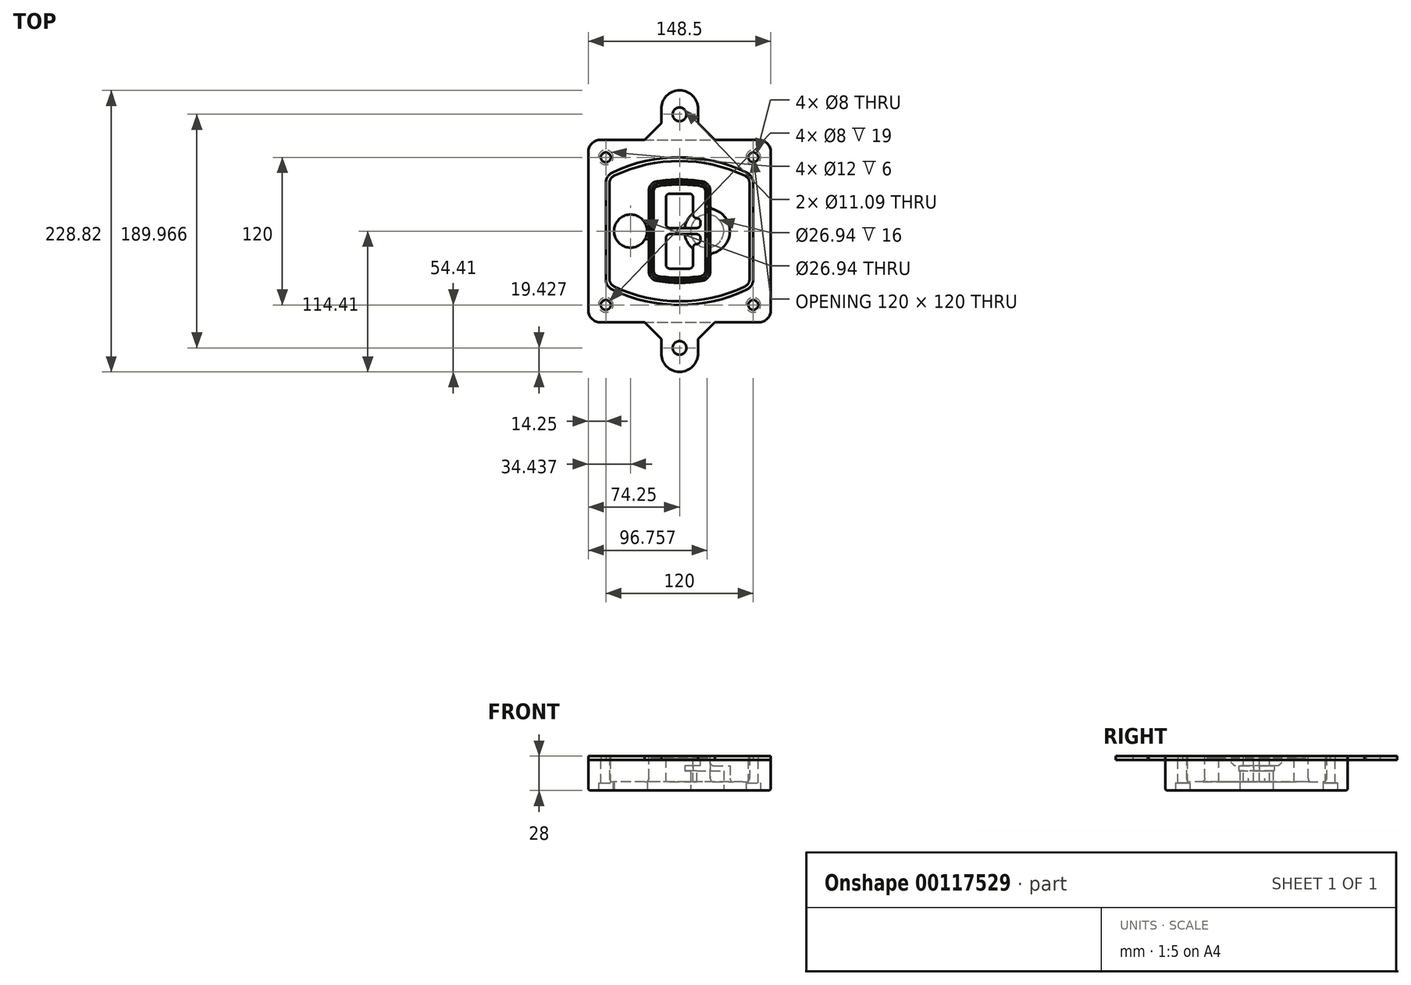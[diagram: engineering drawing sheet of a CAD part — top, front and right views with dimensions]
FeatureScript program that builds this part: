
annotation { "Feature Type Name" : "Feature", "Feature Type Description" : "" }
export const myFeature = defineFeature(function(context is Context, id is Id, definition is map)
    precondition{}
    {
        {
            var Q0;
            Q0=qCreatedBy(makeId("Top.planeOp"),FACE);
            var sketch = newSketch(context, id + "F0", { "sketchPlane" : qUnion([Q0])});
            skPoint(sketch, "E0.rect.middle", {"position": v(0, 0) * mm});
            skLineSegment(sketch, "E1.bottom", {"start": v(-64.25, -74.25) * mm, "end": v(64.25, -74.25) * mm});
            skLineSegment(sketch, "E1.top", {"start": v(-64.25, 74.25) * mm, "end": v(64.25, 74.25) * mm});
            skLineSegment(sketch, "E1.left", {"start": v(-74.25, -64.25) * mm, "end": v(-74.25, 64.25) * mm});
            skLineSegment(sketch, "E1.right", {"start": v(74.25, -64.25) * mm, "end": v(74.25, 64.25) * mm});
            skLineSegment(sketch, "E2", {"start": v(-74.25, 74.25) * mm, "end": v(74.25, -74.25) * mm, "construction": true});
            skLineSegment(sketch, "E3", {"start": v(74.25, 74.25) * mm, "end": v(-74.25, -74.25) * mm, "construction": true});
            skCircle(sketch, "E4", {"center": v(-60, 60) * mm, "radius": 4 * mm});
            skCircle(sketch, "E5", {"center": v(60, 60) * mm, "radius": 4 * mm});
            skCircle(sketch, "E6", {"center": v(60, -60) * mm, "radius": 4 * mm});
            skCircle(sketch, "E7", {"center": v(-60, -60) * mm, "radius": 4 * mm});
            skLineSegment(sketch, "E8", {"start": v(-60, 60) * mm, "end": v(60, 60) * mm, "construction": true});
            skLineSegment(sketch, "E9", {"start": v(60, 60) * mm, "end": v(60, -60) * mm, "construction": true});
            skLineSegment(sketch, "E10", {"start": v(60, -60) * mm, "end": v(-60, -60) * mm, "construction": true});
            skLineSegment(sketch, "E11", {"start": v(-60, -60) * mm, "end": v(-60, 60) * mm, "construction": true});
            skLineSegment(sketch, "E12", {"start": v(-60, 38.83) * mm, "end": v(-60, -38.83) * mm});
            skLineSegment(sketch, "E13", {"start": v(60, 38.83) * mm, "end": v(60, -38.83) * mm});
            skArc(sketch, "E14", {"start": v(54.26, 47.88) * mm, "mid": v(0, 60) * mm, "end": v(-54.26, 47.88) * mm});
            skArc(sketch, "E15", {"start": v(-54.26, -47.88) * mm, "mid": v(0, -60) * mm, "end": v(54.26, -47.88) * mm});
            skLineSegment(sketch, "E16", {"start": v(-60, 0) * mm, "end": v(60, 0) * mm, "construction": true});
            skPoint(sketch, "E17.visualSharp", {"position": v(-60, -45) * mm});
            skArc(sketch, "E17.filletArc", {"start": v(-60, -38.83) * mm, "mid": v(-58.44, -44.2) * mm, "end": v(-54.26, -47.88) * mm});
            skPoint(sketch, "E18.visualSharp", {"position": v(-60, 45) * mm});
            skArc(sketch, "E18.filletArc", {"start": v(-54.26, 47.88) * mm, "mid": v(-58.44, 44.2) * mm, "end": v(-60, 38.83) * mm});
            skPoint(sketch, "E19.visualSharp", {"position": v(60, 45) * mm});
            skArc(sketch, "E19.filletArc", {"start": v(60, 38.83) * mm, "mid": v(58.44, 44.2) * mm, "end": v(54.26, 47.88) * mm});
            skPoint(sketch, "E20.visualSharp", {"position": v(60, -45) * mm});
            skArc(sketch, "E20.filletArc", {"start": v(54.26, -47.88) * mm, "mid": v(58.44, -44.2) * mm, "end": v(60, -38.83) * mm});
            skPoint(sketch, "E21.visualSharp", {"position": v(-74.25, 74.25) * mm});
            skArc(sketch, "E21.filletArc", {"start": v(-64.25, 74.25) * mm, "mid": v(-71.32, 71.32) * mm, "end": v(-74.25, 64.25) * mm});
            skPoint(sketch, "E22.visualSharp", {"position": v(74.25, 74.25) * mm});
            skArc(sketch, "E22.filletArc", {"start": v(74.25, 64.25) * mm, "mid": v(71.32, 71.32) * mm, "end": v(64.25, 74.25) * mm});
            skPoint(sketch, "E23.visualSharp", {"position": v(74.25, -74.25) * mm});
            skArc(sketch, "E23.filletArc", {"start": v(64.25, -74.25) * mm, "mid": v(71.32, -71.32) * mm, "end": v(74.25, -64.25) * mm});
            skPoint(sketch, "E24.visualSharp", {"position": v(-74.25, -74.25) * mm});
            skArc(sketch, "E24.filletArc", {"start": v(-74.25, -64.25) * mm, "mid": v(-71.32, -71.32) * mm, "end": v(-64.25, -74.25) * mm});
            skArc(sketch, "E25.0", {"start": v(57, 38.83) * mm, "mid": v(55.9, 42.58) * mm, "end": v(52.98, 45.17) * mm});
            skLineSegment(sketch, "E25.1", {"start": v(57, 38.83) * mm, "end": v(57, -38.83) * mm});
            skArc(sketch, "E25.2", {"start": v(52.98, -45.17) * mm, "mid": v(55.9, -42.58) * mm, "end": v(57, -38.83) * mm});
            skArc(sketch, "E25.3", {"start": v(-52.98, -45.17) * mm, "mid": v(0, -57) * mm, "end": v(52.98, -45.17) * mm});
            skArc(sketch, "E25.4", {"start": v(-57, -38.83) * mm, "mid": v(-55.9, -42.58) * mm, "end": v(-52.98, -45.17) * mm});
            skArc(sketch, "E25.5", {"start": v(52.98, 45.17) * mm, "mid": v(0, 57) * mm, "end": v(-52.98, 45.17) * mm});
            skLineSegment(sketch, "E25.6", {"start": v(-57, 38.83) * mm, "end": v(-57, -38.83) * mm});
            skArc(sketch, "E25.7", {"start": v(-52.98, 45.17) * mm, "mid": v(-55.9, 42.58) * mm, "end": v(-57, 38.83) * mm});
            skArc(sketch, "E26.0", {"start": v(-55.96, 51.5) * mm, "mid": v(-61.82, 46.33) * mm, "end": v(-64, 38.83) * mm});
            skArc(sketch, "E26.1", {"start": v(55.96, 51.5) * mm, "mid": v(0, 64) * mm, "end": v(-55.96, 51.5) * mm});
            skArc(sketch, "E26.2", {"start": v(64, 38.83) * mm, "mid": v(61.82, 46.33) * mm, "end": v(55.96, 51.5) * mm});
            skLineSegment(sketch, "E26.3", {"start": v(64, 38.83) * mm, "end": v(64, -38.83) * mm});
            skArc(sketch, "E26.4", {"start": v(55.96, -51.5) * mm, "mid": v(61.82, -46.33) * mm, "end": v(64, -38.83) * mm});
            skLineSegment(sketch, "E26.5", {"start": v(-64, 38.83) * mm, "end": v(-64, -38.83) * mm});
            skArc(sketch, "E26.6", {"start": v(-55.96, -51.5) * mm, "mid": v(0, -64) * mm, "end": v(55.96, -51.5) * mm});
            skArc(sketch, "E26.7", {"start": v(-64, -38.83) * mm, "mid": v(-61.82, -46.33) * mm, "end": v(-55.96, -51.5) * mm});
            skSolve(sketch);
        }
        {
            var Q0;
            Q0=makeQuery(id+"F0.imprint","IMPRINT",FACE,{"disambiguationData":[TD([[makeQuery(id+"F0.imprint","IMPRINT",EDGE,{"derivedFrom":sQuery(id+"F0.wireOp",EDGE,"E1.bottom")}),1.0]])]});
            var Q1;
            Q1=makeQuery(id+"F0.imprint","IMPRINT",FACE,{"disambiguationData":[TD([[makeQuery(id+"F0.imprint","IMPRINT",EDGE,{"derivedFrom":sQuery(id+"F0.wireOp",EDGE,"E12")}),1.0]])]});
            var Q2;
            Q2=makeQuery(id+"F0.imprint","IMPRINT",FACE,{"disambiguationData":[TD([[makeQuery(id+"F0.imprint","IMPRINT",EDGE,{"derivedFrom":sQuery(id+"F0.wireOp",EDGE,"E25.0")}),1.0]])]});
            var Q3;
            Q3=makeQuery(id+"F0.imprint","IMPRINT",FACE,{"disambiguationData":[TD([[makeQuery(id+"F0.imprint","IMPRINT",EDGE,{"derivedFrom":sQuery(id+"F0.wireOp",EDGE,"E12")}),-1.0]])]});
            extrude(context, id + "F1", {"entities" : qUnion([Q0, Q1, Q2, Q3]), "oppositeDirection" : true, "depth" : 25 * mm});
        }
        {
            var Q0;
            Q0=makeQuery(id+"F0.imprint","IMPRINT",FACE,{"disambiguationData":[TD([[makeQuery(id+"F0.imprint","IMPRINT",EDGE,{"derivedFrom":sQuery(id+"F0.wireOp",EDGE,"E12")}),1.0]])]});
            extrude(context, id + "F2", {"entities" : qUnion([Q0]), "operationType" : NewBodyOperationType.ADD, "depth" : 3 * mm});
        }
        {
            var Q0;
            Q0=makeQuery(id+"F0.imprint","IMPRINT",FACE,{"disambiguationData":[TD([[makeQuery(id+"F0.imprint","IMPRINT",EDGE,{"derivedFrom":sQuery(id+"F0.wireOp",EDGE,"E25.0")}),1.0]])]});
            extrude(context, id + "F3", {"entities" : qUnion([Q0]), "operationType" : NewBodyOperationType.REMOVE, "oppositeDirection" : true, "depth" : 18 * mm});
        }
        {
            var Q0;
            Q0=makeQuery(id+"F2.opExtrude","CAP_FACE",FACE,{"disambiguationData":[OSD([sQuery(id+"F0.wireOp",EDGE,"E12"),sQuery(id+"F0.wireOp",EDGE,"E13"),sQuery(id+"F0.wireOp",EDGE,"E14"),sQuery(id+"F0.wireOp",EDGE,"E15"),sQuery(id+"F0.wireOp",EDGE,"E17.filletArc"),sQuery(id+"F0.wireOp",EDGE,"E18.filletArc"),sQuery(id+"F0.wireOp",EDGE,"E19.filletArc"),sQuery(id+"F0.wireOp",EDGE,"E20.filletArc"),sQuery(id+"F0.wireOp",EDGE,"E25.0"),sQuery(id+"F0.wireOp",EDGE,"E25.1"),sQuery(id+"F0.wireOp",EDGE,"E25.2"),sQuery(id+"F0.wireOp",EDGE,"E25.3"),sQuery(id+"F0.wireOp",EDGE,"E25.4"),sQuery(id+"F0.wireOp",EDGE,"E25.5"),sQuery(id+"F0.wireOp",EDGE,"E25.6"),sQuery(id+"F0.wireOp",EDGE,"E25.7")])],"isStart":false});
            var sketch = newSketch(context, id + "F4", { "sketchPlane" : qUnion([Q0])});
            skArc(sketch, "E27.0", {"start": v(-18.34, -40.45) * mm, "mid": v(0, -42) * mm, "end": v(18.34, -40.45) * mm});
            skArc(sketch, "E28.0", {"start": v(18.34, 40.45) * mm, "mid": v(0, 42) * mm, "end": v(-18.34, 40.45) * mm});
            skLineSegment(sketch, "E29", {"start": v(-25, 32.57) * mm, "end": v(-25, -32.57) * mm});
            skLineSegment(sketch, "E30", {"start": v(25, 32.57) * mm, "end": v(25, -32.57) * mm});
            skLineSegment(sketch, "E31", {"start": v(-25, 39.1) * mm, "end": v(25, 39.1) * mm, "construction": true});
            skLineSegment(sketch, "E32", {"start": v(-25, -39.1) * mm, "end": v(25, -39.1) * mm, "construction": true});
            skPoint(sketch, "E33.visualSharp", {"position": v(-25, 39.1) * mm});
            skArc(sketch, "E33.filletArc", {"start": v(-18.34, 40.45) * mm, "mid": v(-23.11, 37.73) * mm, "end": v(-25, 32.57) * mm});
            skPoint(sketch, "E34.visualSharp", {"position": v(25, 39.1) * mm});
            skArc(sketch, "E34.filletArc", {"start": v(25, 32.57) * mm, "mid": v(23.11, 37.73) * mm, "end": v(18.34, 40.45) * mm});
            skPoint(sketch, "E35.visualSharp", {"position": v(25, -39.1) * mm});
            skArc(sketch, "E35.filletArc", {"start": v(18.34, -40.45) * mm, "mid": v(23.11, -37.73) * mm, "end": v(25, -32.57) * mm});
            skPoint(sketch, "E36.visualSharp", {"position": v(-25, -39.1) * mm});
            skArc(sketch, "E36.filletArc", {"start": v(-25, -32.57) * mm, "mid": v(-23.11, -37.73) * mm, "end": v(-18.34, -40.45) * mm});
            skArc(sketch, "E37.0", {"start": v(52.98, 45.17) * mm, "mid": v(0, 57) * mm, "end": v(-52.98, 45.17) * mm});
            skArc(sketch, "E37.1", {"start": v(-52.98, 45.17) * mm, "mid": v(-55.9, 42.58) * mm, "end": v(-57, 38.83) * mm});
            skLineSegment(sketch, "E37.2", {"start": v(-57, 38.83) * mm, "end": v(-57, -38.83) * mm});
            skArc(sketch, "E37.3", {"start": v(-57, -38.83) * mm, "mid": v(-55.9, -42.58) * mm, "end": v(-52.98, -45.17) * mm});
            skArc(sketch, "E37.4", {"start": v(-52.98, -45.17) * mm, "mid": v(0, -57) * mm, "end": v(52.98, -45.17) * mm});
            skArc(sketch, "E37.5", {"start": v(52.98, -45.17) * mm, "mid": v(55.9, -42.58) * mm, "end": v(57, -38.83) * mm});
            skLineSegment(sketch, "E37.6", {"start": v(57, 38.83) * mm, "end": v(57, -38.83) * mm});
            skArc(sketch, "E37.7", {"start": v(57, 38.83) * mm, "mid": v(55.9, 42.58) * mm, "end": v(52.98, 45.17) * mm});
            skLineSegment(sketch, "E38.0", {"start": v(23, 32.57) * mm, "end": v(23, -32.57) * mm});
            skArc(sketch, "E38.1", {"start": v(18, -38.48) * mm, "mid": v(21.58, -36.44) * mm, "end": v(23, -32.57) * mm});
            skArc(sketch, "E38.2", {"start": v(-18, -38.48) * mm, "mid": v(0, -40) * mm, "end": v(18, -38.48) * mm});
            skArc(sketch, "E38.3", {"start": v(-23, -32.57) * mm, "mid": v(-21.58, -36.44) * mm, "end": v(-18, -38.48) * mm});
            skLineSegment(sketch, "E38.4", {"start": v(-23, 32.57) * mm, "end": v(-23, -32.57) * mm});
            skArc(sketch, "E38.5", {"start": v(23, 32.57) * mm, "mid": v(21.58, 36.44) * mm, "end": v(18, 38.48) * mm});
            skArc(sketch, "E38.6", {"start": v(-18, 38.48) * mm, "mid": v(-21.58, 36.44) * mm, "end": v(-23, 32.57) * mm});
            skArc(sketch, "E38.7", {"start": v(18, 38.48) * mm, "mid": v(0, 40) * mm, "end": v(-18, 38.48) * mm});
            skArc(sketch, "E39.0", {"start": v(21, 32.57) * mm, "mid": v(20.06, 35.15) * mm, "end": v(17.67, 36.5) * mm});
            skLineSegment(sketch, "E39.1", {"start": v(21, 32.57) * mm, "end": v(21, -32.57) * mm});
            skArc(sketch, "E39.2", {"start": v(17.67, -36.5) * mm, "mid": v(20.06, -35.15) * mm, "end": v(21, -32.57) * mm});
            skArc(sketch, "E39.3", {"start": v(-17.67, -36.5) * mm, "mid": v(0, -38) * mm, "end": v(17.67, -36.5) * mm});
            skArc(sketch, "E39.4", {"start": v(-21, -32.57) * mm, "mid": v(-20.06, -35.15) * mm, "end": v(-17.67, -36.5) * mm});
            skArc(sketch, "E39.5", {"start": v(17.67, 36.5) * mm, "mid": v(0, 38) * mm, "end": v(-17.67, 36.5) * mm});
            skLineSegment(sketch, "E39.6", {"start": v(-21, 32.57) * mm, "end": v(-21, -32.57) * mm});
            skArc(sketch, "E39.7", {"start": v(-17.67, 36.5) * mm, "mid": v(-20.06, 35.15) * mm, "end": v(-21, 32.57) * mm});
            skLineSegment(sketch, "E40", {"start": v(-25, 0) * mm, "end": v(25, 0) * mm, "construction": true});
            skLineSegment(sketch, "E41", {"start": v(-11, 5.5) * mm, "end": v(-11, 27.5) * mm});
            skLineSegment(sketch, "E42", {"start": v(-8, 30.5) * mm, "end": v(8, 30.5) * mm});
            skLineSegment(sketch, "E43", {"start": v(11, 27.5) * mm, "end": v(11, 13.5) * mm});
            skLineSegment(sketch, "E44", {"start": v(14, 10.5) * mm, "end": v(14, 10.5) * mm});
            skLineSegment(sketch, "E45", {"start": v(17, 7.5) * mm, "end": v(17, 5.5) * mm});
            skLineSegment(sketch, "E46", {"start": v(14, 2.5) * mm, "end": v(-8, 2.5) * mm});
            skPoint(sketch, "E47.visualSharp", {"position": v(-11, 30.5) * mm});
            skArc(sketch, "E47.filletArc", {"start": v(-8, 30.5) * mm, "mid": v(-10.12, 29.62) * mm, "end": v(-11, 27.5) * mm});
            skPoint(sketch, "E48.visualSharp", {"position": v(11, 30.5) * mm});
            skArc(sketch, "E48.filletArc", {"start": v(11, 27.5) * mm, "mid": v(10.12, 29.62) * mm, "end": v(8, 30.5) * mm});
            skPoint(sketch, "E49.visualSharp", {"position": v(11, 10.5) * mm});
            skArc(sketch, "E49.filletArc", {"start": v(11, 13.5) * mm, "mid": v(11.88, 11.38) * mm, "end": v(14, 10.5) * mm});
            skPoint(sketch, "E50.visualSharp", {"position": v(17, 10.5) * mm});
            skArc(sketch, "E50.filletArc", {"start": v(17, 7.5) * mm, "mid": v(16.12, 9.62) * mm, "end": v(14, 10.5) * mm});
            skPoint(sketch, "E51.visualSharp", {"position": v(17, 2.5) * mm});
            skArc(sketch, "E51.filletArc", {"start": v(14, 2.5) * mm, "mid": v(16.12, 3.38) * mm, "end": v(17, 5.5) * mm});
            skPoint(sketch, "E52.visualSharp", {"position": v(-11, 2.5) * mm});
            skArc(sketch, "E52.filletArc", {"start": v(-11, 5.5) * mm, "mid": v(-10.12, 3.38) * mm, "end": v(-8, 2.5) * mm});
            skLineSegment(sketch, "E53.0.MirrorCS", {"start": v(14, -2.5) * mm, "end": v(-8, -2.5) * mm});
            skArc(sketch, "E54.0.MirrorCS", {"start": v(-11, -5.5) * mm, "mid": v(-10.12, -3.38) * mm, "end": v(-8, -2.5) * mm});
            skLineSegment(sketch, "E55.0.MirrorCS", {"start": v(-11, -5.5) * mm, "end": v(-11, -27.5) * mm});
            skArc(sketch, "E56.0.MirrorCS", {"start": v(-8, -30.5) * mm, "mid": v(-10.12, -29.62) * mm, "end": v(-11, -27.5) * mm});
            skLineSegment(sketch, "E57.0.MirrorCS", {"start": v(-8, -30.5) * mm, "end": v(8, -30.5) * mm});
            skArc(sketch, "E58.0.MirrorCS", {"start": v(11, -27.5) * mm, "mid": v(10.12, -29.62) * mm, "end": v(8, -30.5) * mm});
            skLineSegment(sketch, "E59.0.MirrorCS", {"start": v(11, -27.5) * mm, "end": v(11, -13.5) * mm});
            skArc(sketch, "E60.0.MirrorCS", {"start": v(11, -13.5) * mm, "mid": v(11.88, -11.38) * mm, "end": v(14, -10.5) * mm});
            skArc(sketch, "E61.0.MirrorCS", {"start": v(17, -7.5) * mm, "mid": v(16.12, -9.62) * mm, "end": v(14, -10.5) * mm});
            skLineSegment(sketch, "E62.0.MirrorCS", {"start": v(17, -7.5) * mm, "end": v(17, -5.5) * mm});
            skArc(sketch, "E63.0.MirrorCS", {"start": v(14, -2.5) * mm, "mid": v(16.12, -3.38) * mm, "end": v(17, -5.5) * mm});
            skSolve(sketch);
        }
        {
            var Q0;
            Q0=makeQuery(id+"F4.imprint","IMPRINT",FACE,{"disambiguationData":[TD([[makeQuery(id+"F4.imprint","IMPRINT",EDGE,{"derivedFrom":sQuery(id+"F4.wireOp",EDGE,"E27.0")}),1.0]])]});
            var Q1;
            Q1=makeQuery(id+"F4.imprint","IMPRINT",FACE,{"disambiguationData":[TD([[makeQuery(id+"F4.imprint","IMPRINT",EDGE,{"derivedFrom":sQuery(id+"F4.wireOp",EDGE,"E38.0")}),-1.0]])]});
            var Q2;
            Q2=makeQuery(id+"F4.imprint","IMPRINT",FACE,{"disambiguationData":[TD([[makeQuery(id+"F4.imprint","IMPRINT",EDGE,{"derivedFrom":sQuery(id+"F4.wireOp",EDGE,"E39.0")}),1.0]])]});
            extrude(context, id + "F5", {"entities" : qUnion([Q0, Q1, Q2]), "operationType" : NewBodyOperationType.ADD, "endBound" : BoundingType.UP_TO_NEXT, "oppositeDirection" : true, "depth" : 25 * mm});
        }
        {
            var Q0;
            Q0=makeQuery(id+"F4.imprint","IMPRINT",FACE,{"disambiguationData":[TD([[makeQuery(id+"F4.imprint","IMPRINT",EDGE,{"derivedFrom":sQuery(id+"F4.wireOp",EDGE,"E38.0")}),-1.0]])]});
            extrude(context, id + "F6", {"entities" : qUnion([Q0]), "operationType" : NewBodyOperationType.REMOVE, "oppositeDirection" : true, "depth" : 2 * mm});
        }
        {
            var Q0;
            Q0=makeQuery(id+"F1.opExtrude","CAP_FACE",FACE,{"disambiguationData":[OSD([sQuery(id+"F0.wireOp",EDGE,"E1.bottom"),sQuery(id+"F0.wireOp",EDGE,"E1.top"),sQuery(id+"F0.wireOp",EDGE,"E1.left"),sQuery(id+"F0.wireOp",EDGE,"E1.right"),sQuery(id+"F0.wireOp",EDGE,"E4"),sQuery(id+"F0.wireOp",EDGE,"E5"),sQuery(id+"F0.wireOp",EDGE,"E6"),sQuery(id+"F0.wireOp",EDGE,"E7"),sQuery(id+"F0.wireOp",EDGE,"E21.filletArc"),sQuery(id+"F0.wireOp",EDGE,"E22.filletArc"),sQuery(id+"F0.wireOp",EDGE,"E23.filletArc"),sQuery(id+"F0.wireOp",EDGE,"E24.filletArc")])],"isStart":false});
            var sketch = newSketch(context, id + "F7", { "sketchPlane" : qUnion([Q0])});
            skCircle(sketch, "E64", {"center": v(22.5, 0) * mm, "radius": 13.47 * mm});
            skCircle(sketch, "E65", {"center": v(-39.81, 0) * mm, "radius": 13.47 * mm});
            skLineSegment(sketch, "E66", {"start": v(74.25, 0) * mm, "end": v(-74.25, 0) * mm});
            skCircle(sketch, "E67", {"center": v(22.5, 0) * mm, "radius": 18.47 * mm});
            skCircle(sketch, "E68", {"center": v(60, -60) * mm, "radius": 6 * mm});
            skCircle(sketch, "E69", {"center": v(-60, -60) * mm, "radius": 6 * mm});
            skCircle(sketch, "E70", {"center": v(-60, 60) * mm, "radius": 6 * mm});
            skCircle(sketch, "E71", {"center": v(60, 60) * mm, "radius": 6 * mm});
            skSolve(sketch);
        }
        {
            var Q0;
            {var subQ1=sQuery(id+"F7.wireOp",EDGE,"E66");var subQ4=sQuery(id+"F7.wireOp",EDGE,"E64");var subQ6=makeQuery(id+"F7.imprint","INTERSECT",VERTEX,{"disambiguationData":[OD(0.0)],"derivedFrom":[subQ4,subQ1]});Q0=makeQuery(id+"F7.imprint","IMPRINT",FACE,{"disambiguationData":[TD([[makeQuery(id+"F7.imprint","IMPRINT",EDGE,{"disambiguationData":[TD([[subQ6,-1.0]])],"derivedFrom":subQ4}),-1.0]])]});}
            var Q1;
            {var subQ0=sQuery(id+"F7.wireOp",EDGE,"E66");var subQ1=sQuery(id+"F7.wireOp",EDGE,"E64");var subQ3=makeQuery(id+"F7.imprint","INTERSECT",VERTEX,{"disambiguationData":[OD(0.0)],"derivedFrom":[subQ1,subQ0]});Q1=makeQuery(id+"F7.imprint","IMPRINT",FACE,{"disambiguationData":[TD([[makeQuery(id+"F7.imprint","IMPRINT",EDGE,{"disambiguationData":[TD([[subQ3,-1.0]])],"derivedFrom":subQ1}),1.0]])]});}
            var Q2;
            {var subQ0=sQuery(id+"F7.wireOp",EDGE,"E66");var subQ1=sQuery(id+"F7.wireOp",EDGE,"E64");var subQ3=makeQuery(id+"F7.imprint","INTERSECT",VERTEX,{"disambiguationData":[OD(0.0)],"derivedFrom":[subQ1,subQ0]});Q2=makeQuery(id+"F7.imprint","IMPRINT",FACE,{"disambiguationData":[TD([[makeQuery(id+"F7.imprint","IMPRINT",EDGE,{"disambiguationData":[TD([[subQ3,1.0]])],"derivedFrom":subQ1}),1.0]])]});}
            var Q3;
            {var subQ1=sQuery(id+"F7.wireOp",EDGE,"E66");var subQ4=sQuery(id+"F7.wireOp",EDGE,"E64");var subQ6=makeQuery(id+"F7.imprint","INTERSECT",VERTEX,{"disambiguationData":[OD(0.0)],"derivedFrom":[subQ4,subQ1]});Q3=makeQuery(id+"F7.imprint","IMPRINT",FACE,{"disambiguationData":[TD([[makeQuery(id+"F7.imprint","IMPRINT",EDGE,{"disambiguationData":[TD([[subQ6,1.0]])],"derivedFrom":subQ4}),-1.0]])]});}
            extrude(context, id + "F8", {"entities" : qUnion([Q0, Q1, Q2, Q3]), "operationType" : NewBodyOperationType.ADD, "oppositeDirection" : true, "depth" : 20 * mm});
        }
        {
            var Q0;
            {var subQ0=sQuery(id+"F7.wireOp",EDGE,"E66");var subQ1=sQuery(id+"F7.wireOp",EDGE,"E64");var subQ3=makeQuery(id+"F7.imprint","INTERSECT",VERTEX,{"disambiguationData":[OD(0.0)],"derivedFrom":[subQ1,subQ0]});Q0=makeQuery(id+"F7.imprint","IMPRINT",FACE,{"disambiguationData":[TD([[makeQuery(id+"F7.imprint","IMPRINT",EDGE,{"disambiguationData":[TD([[subQ3,-1.0]])],"derivedFrom":subQ1}),1.0]])]});}
            var Q1;
            {var subQ0=sQuery(id+"F7.wireOp",EDGE,"E66");var subQ1=sQuery(id+"F7.wireOp",EDGE,"E64");var subQ3=makeQuery(id+"F7.imprint","INTERSECT",VERTEX,{"disambiguationData":[OD(0.0)],"derivedFrom":[subQ1,subQ0]});Q1=makeQuery(id+"F7.imprint","IMPRINT",FACE,{"disambiguationData":[TD([[makeQuery(id+"F7.imprint","IMPRINT",EDGE,{"disambiguationData":[TD([[subQ3,1.0]])],"derivedFrom":subQ1}),1.0]])]});}
            extrude(context, id + "F9", {"entities" : qUnion([Q0, Q1]), "operationType" : NewBodyOperationType.REMOVE, "oppositeDirection" : true, "depth" : 16 * mm});
        }
        {
            var Q0;
            {var subQ0=sQuery(id+"F7.wireOp",EDGE,"E66");var subQ1=sQuery(id+"F7.wireOp",EDGE,"E65");var subQ3=makeQuery(id+"F7.imprint","INTERSECT",VERTEX,{"disambiguationData":[OD(0.0)],"derivedFrom":[subQ1,subQ0]});Q0=makeQuery(id+"F7.imprint","IMPRINT",FACE,{"disambiguationData":[TD([[makeQuery(id+"F7.imprint","IMPRINT",EDGE,{"disambiguationData":[TD([[subQ3,-1.0]])],"derivedFrom":subQ1}),1.0]])]});}
            var Q1;
            {var subQ0=sQuery(id+"F7.wireOp",EDGE,"E66");var subQ1=sQuery(id+"F7.wireOp",EDGE,"E65");var subQ3=makeQuery(id+"F7.imprint","INTERSECT",VERTEX,{"disambiguationData":[OD(0.0)],"derivedFrom":[subQ1,subQ0]});Q1=makeQuery(id+"F7.imprint","IMPRINT",FACE,{"disambiguationData":[TD([[makeQuery(id+"F7.imprint","IMPRINT",EDGE,{"disambiguationData":[TD([[subQ3,1.0]])],"derivedFrom":subQ1}),1.0]])]});}
            extrude(context, id + "F10", {"entities" : qUnion([Q0, Q1]), "operationType" : NewBodyOperationType.REMOVE, "oppositeDirection" : true, "depth" : 25 * mm});
        }
        {
            var Q0;
            Q0=makeQuery(id+"F7.imprint","IMPRINT",FACE,{"disambiguationData":[TD([[makeQuery(id+"F7.imprint","IMPRINT",EDGE,{"derivedFrom":sQuery(id+"F7.wireOp",EDGE,"E68")}),1.0]])]});
            var Q1;
            Q1=makeQuery(id+"F7.imprint","IMPRINT",FACE,{"disambiguationData":[TD([[makeQuery(id+"F7.imprint","IMPRINT",EDGE,{"derivedFrom":makeQuery(id+"F1.opExtrude","CAP_EDGE",EDGE,{"disambiguationData":[OSD([sQuery(id+"F0.wireOp",EDGE,"E5")])],"isStart":false})}),-1.0]])]});
            var Q2;
            Q2=makeQuery(id+"F7.imprint","IMPRINT",FACE,{"disambiguationData":[TD([[makeQuery(id+"F7.imprint","IMPRINT",EDGE,{"derivedFrom":sQuery(id+"F7.wireOp",EDGE,"E69")}),1.0]])]});
            var Q3;
            Q3=makeQuery(id+"F7.imprint","IMPRINT",FACE,{"disambiguationData":[TD([[makeQuery(id+"F7.imprint","IMPRINT",EDGE,{"derivedFrom":makeQuery(id+"F1.opExtrude","CAP_EDGE",EDGE,{"disambiguationData":[OSD([sQuery(id+"F0.wireOp",EDGE,"E4")])],"isStart":false})}),-1.0]])]});
            var Q4;
            Q4=makeQuery(id+"F7.imprint","IMPRINT",FACE,{"disambiguationData":[TD([[makeQuery(id+"F7.imprint","IMPRINT",EDGE,{"derivedFrom":sQuery(id+"F7.wireOp",EDGE,"E70")}),1.0]])]});
            var Q5;
            Q5=makeQuery(id+"F7.imprint","IMPRINT",FACE,{"disambiguationData":[TD([[makeQuery(id+"F7.imprint","IMPRINT",EDGE,{"derivedFrom":makeQuery(id+"F1.opExtrude","CAP_EDGE",EDGE,{"disambiguationData":[OSD([sQuery(id+"F0.wireOp",EDGE,"E7")])],"isStart":false})}),-1.0]])]});
            var Q6;
            Q6=makeQuery(id+"F7.imprint","IMPRINT",FACE,{"disambiguationData":[TD([[makeQuery(id+"F7.imprint","IMPRINT",EDGE,{"derivedFrom":sQuery(id+"F7.wireOp",EDGE,"E71")}),1.0]])]});
            var Q7;
            Q7=makeQuery(id+"F7.imprint","IMPRINT",FACE,{"disambiguationData":[TD([[makeQuery(id+"F7.imprint","IMPRINT",EDGE,{"derivedFrom":makeQuery(id+"F1.opExtrude","CAP_EDGE",EDGE,{"disambiguationData":[OSD([sQuery(id+"F0.wireOp",EDGE,"E6")])],"isStart":false})}),-1.0]])]});
            extrude(context, id + "F11", {"entities" : qUnion([Q0, Q1, Q2, Q3, Q4, Q5, Q6, Q7]), "operationType" : NewBodyOperationType.REMOVE, "oppositeDirection" : true, "depth" : 6 * mm});
        }
        {
            var Q0;
            Q0=makeQuery(id+"F9.boolean.opBoolean","COPY",FACE,{"derivedFrom":makeQuery(id+"F9.opExtrude","CAP_FACE",FACE,{"disambiguationData":[OSD([sQuery(id+"F7.wireOp",EDGE,"E64")])],"isStart":false})});
            var sketch = newSketch(context, id + "F12", { "sketchPlane" : qUnion([Q0])});
            skArc(sketch, "E72.0", {"start": v(11, 14.45) * mm, "mid": v(6.45, 9.13) * mm, "end": v(4.2, 2.5) * mm});
            skArc(sketch, "E72.1", {"start": v(4.2, -2.5) * mm, "mid": v(6.45, -9.13) * mm, "end": v(11, -14.45) * mm});
            skLineSegment(sketch, "E73", {"start": v(4.2, -2.5) * mm, "end": v(14, -2.5) * mm});
            skLineSegment(sketch, "E74.0", {"start": v(14, 2.5) * mm, "end": v(4.2, 2.5) * mm});
            skArc(sketch, "E74.1", {"start": v(14, 2.5) * mm, "mid": v(16.12, 3.38) * mm, "end": v(17, 5.5) * mm});
            skLineSegment(sketch, "E74.2", {"start": v(17, 7.5) * mm, "end": v(17, 5.5) * mm});
            skArc(sketch, "E74.3", {"start": v(17, 7.5) * mm, "mid": v(16.12, 9.62) * mm, "end": v(14, 10.5) * mm});
            skArc(sketch, "E74.4", {"start": v(11, 13.5) * mm, "mid": v(11.88, 11.38) * mm, "end": v(14, 10.5) * mm});
            skLineSegment(sketch, "E74.5", {"start": v(11, 14.45) * mm, "end": v(11, 13.5) * mm});
            skLineSegment(sketch, "E74.7", {"start": v(14, -2.5) * mm, "end": v(4.2, -2.5) * mm});
            skArc(sketch, "E74.8", {"start": v(14, -2.5) * mm, "mid": v(16.12, -3.38) * mm, "end": v(17, -5.5) * mm});
            skLineSegment(sketch, "E74.9", {"start": v(17, -7.5) * mm, "end": v(17, -5.5) * mm});
            skArc(sketch, "E74.10", {"start": v(17, -7.5) * mm, "mid": v(16.12, -9.62) * mm, "end": v(14, -10.5) * mm});
            skArc(sketch, "E74.11", {"start": v(11, -13.5) * mm, "mid": v(11.88, -11.38) * mm, "end": v(14, -10.5) * mm});
            skLineSegment(sketch, "E74.12", {"start": v(11, -14.45) * mm, "end": v(11, -13.5) * mm});
            skPoint(sketch, "E75.orphan", {"position": v(11, -27.5) * mm});
            skPoint(sketch, "E76.orphan", {"position": v(-8, -2.5) * mm});
            skPoint(sketch, "E77.orphan", {"position": v(-8, 2.5) * mm});
            skPoint(sketch, "E78.orphan", {"position": v(11, 27.5) * mm});
            skSolve(sketch);
        }
        {
            var Q0;
            {var subQ7=sQuery(id+"F12.wireOp",EDGE,"E72.0");var subQ14=sQuery(id+"F12.wireOp",EDGE,"E72.1");var subQ16=sQuery(id+"F12.wireOp",EDGE,"E74.1");var subQ18=sQuery(id+"F12.wireOp",EDGE,"E74.8");Q0=qUnion([makeQuery(id+"F12.imprint","IMPRINT",FACE,{"disambiguationData":[TD([[makeQuery(id+"F12.imprint","IMPRINT",EDGE,{"derivedFrom":subQ7}),1.0]])]}),makeQuery(id+"F12.imprint","IMPRINT",FACE,{"disambiguationData":[TD([[makeQuery(id+"F12.imprint","IMPRINT",EDGE,{"derivedFrom":subQ14}),1.0]])]}),makeQuery(id+"F12.imprint","IMPRINT",FACE,{"disambiguationData":[TD([[makeQuery(id+"F12.imprint","IMPRINT",EDGE,{"derivedFrom":subQ16}),1.0]])]}),makeQuery(id+"F12.imprint","IMPRINT",FACE,{"disambiguationData":[TD([[makeQuery(id+"F12.imprint","IMPRINT",EDGE,{"derivedFrom":subQ18}),-1.0]])]})]);}
            var Q1;
            Q1=makeQuery(id+"F5.boolean.opBoolean","SPLIT",FACE,{"disambiguationData":[TD([makeQuery(id+"F5.opExtrude","SWEPT_FACE",FACE,{"disambiguationData":[OSD([sQuery(id+"F4.wireOp",EDGE,"E41")])]})])],"derivedFrom":makeQuery(id+"F3.boolean.opBoolean","COPY",FACE,{"derivedFrom":makeQuery(id+"F3.opExtrude","CAP_FACE",FACE,{"disambiguationData":[OSD([sQuery(id+"F0.wireOp",EDGE,"E25.0"),sQuery(id+"F0.wireOp",EDGE,"E25.1"),sQuery(id+"F0.wireOp",EDGE,"E25.2"),sQuery(id+"F0.wireOp",EDGE,"E25.3"),sQuery(id+"F0.wireOp",EDGE,"E25.4"),sQuery(id+"F0.wireOp",EDGE,"E25.5"),sQuery(id+"F0.wireOp",EDGE,"E25.6"),sQuery(id+"F0.wireOp",EDGE,"E25.7")])],"isStart":false})})});
            extrude(context, id + "F13", {"entities" : qUnion([Q0]), "operationType" : NewBodyOperationType.REMOVE, "endBound" : BoundingType.UP_TO_SURFACE, "endBoundEntityFace" : qUnion([Q1]), "depth" : 25 * mm});
        }
        {
            var Q0;
            Q0=makeQuery(id+"F3.boolean.opBoolean","COPY",EDGE,{"derivedFrom":makeQuery(id+"F3.opExtrude","CAP_EDGE",EDGE,{"disambiguationData":[OSD([sQuery(id+"F0.wireOp",EDGE,"E25.6")])],"isStart":false})});
            var Q1;
            Q1=makeQuery(id+"F8.boolean.opBoolean","INTERSECT",EDGE,{"derivedFrom":[makeQuery(id+"F5.opExtrude","SWEPT_FACE",FACE,{"disambiguationData":[OSD([sQuery(id+"F4.wireOp",EDGE,"E30")])]}),makeQuery(id+"F8.opExtrude","CAP_FACE",FACE,{"disambiguationData":[OSD([sQuery(id+"F7.wireOp",EDGE,"E67")])],"isStart":false})]});
            var Q2;
            Q2=makeQuery(id+"F8.boolean.opBoolean","INTERSECT",EDGE,{"disambiguationData":[OD(1.0)],"derivedFrom":[makeQuery(id+"F5.opExtrude","SWEPT_FACE",FACE,{"disambiguationData":[OSD([sQuery(id+"F4.wireOp",EDGE,"E30")])]}),makeQuery(id+"F8.opExtrude","SWEPT_FACE",FACE,{"disambiguationData":[OSD([sQuery(id+"F7.wireOp",EDGE,"E67")])]})]});
            var Q3;
            {var subQ0=sQuery(id+"F4.wireOp",EDGE,"E30");Q3=makeQuery(id+"F8.boolean.opBoolean","SPLIT",EDGE,{"disambiguationData":[TD([makeQuery(id+"F5.opExtrude","SWEPT_FACE",FACE,{"disambiguationData":[OSD([sQuery(id+"F4.wireOp",EDGE,"E35.filletArc")])]})])],"derivedFrom":makeQuery(id+"F5.opExtrude","CAP_EDGE",EDGE,{"disambiguationData":[OSD([subQ0])],"isStart":false})});}
            var Q4;
            {var subQ0=sQuery(id+"F0.wireOp",EDGE,"E25.7");var subQ1=sQuery(id+"F0.wireOp",EDGE,"E25.1");var subQ2=sQuery(id+"F0.wireOp",EDGE,"E25.6");var subQ3=sQuery(id+"F0.wireOp",EDGE,"E25.5");var subQ4=sQuery(id+"F0.wireOp",EDGE,"E25.4");var subQ5=sQuery(id+"F0.wireOp",EDGE,"E25.0");var subQ6=sQuery(id+"F0.wireOp",EDGE,"E25.2");var subQ7=sQuery(id+"F0.wireOp",EDGE,"E25.3");Q4=makeQuery(id+"F8.boolean.opBoolean","INTERSECT",EDGE,{"derivedFrom":[makeQuery(id+"F5.boolean.opBoolean","SPLIT",FACE,{"disambiguationData":[TD([makeQuery(id+"F2.opExtrude","SWEPT_FACE",FACE,{"disambiguationData":[OSD([subQ5])]})])],"derivedFrom":makeQuery(id+"F3.boolean.opBoolean","COPY",FACE,{"derivedFrom":makeQuery(id+"F3.opExtrude","CAP_FACE",FACE,{"disambiguationData":[OSD([subQ5,subQ1,subQ6,subQ7,subQ4,subQ3,subQ2,subQ0])],"isStart":false})})}),makeQuery(id+"F8.opExtrude","SWEPT_FACE",FACE,{"disambiguationData":[OSD([sQuery(id+"F7.wireOp",EDGE,"E67")])]})]});}
            var Q5;
            Q5=makeQuery(id+"F8.boolean.opBoolean","INTERSECT",EDGE,{"disambiguationData":[OD(0.0)],"derivedFrom":[makeQuery(id+"F5.opExtrude","SWEPT_FACE",FACE,{"disambiguationData":[OSD([sQuery(id+"F4.wireOp",EDGE,"E30")])]}),makeQuery(id+"F8.opExtrude","SWEPT_FACE",FACE,{"disambiguationData":[OSD([sQuery(id+"F7.wireOp",EDGE,"E67")])]})]});
            fillet(context, id + "F14", {"entities" : qUnion([Q0, Q1, Q2, Q3, Q4, Q5]), "radius" : 3 * mm, "tangentPropagation" : true, "allowEdgeOverflow" : false});
        }
        {
            var Q0;
            Q0=makeQuery(id+"F1.opExtrude","CAP_EDGE",EDGE,{"disambiguationData":[OSD([sQuery(id+"F0.wireOp",EDGE,"E1.bottom")])],"isStart":false});
            fillet(context, id + "F15", {"entities" : qUnion([Q0]), "radius" : 2 * mm, "tangentPropagation" : true, "allowEdgeOverflow" : false});
        }
        {
            var Q0;
            {var subQ0=sQuery(id+"F0.wireOp",EDGE,"E22.filletArc");var subQ1=sQuery(id+"F0.wireOp",EDGE,"E7");var subQ2=sQuery(id+"F0.wireOp",EDGE,"E6");var subQ3=sQuery(id+"F0.wireOp",EDGE,"E5");var subQ4=sQuery(id+"F0.wireOp",EDGE,"E4");var subQ5=sQuery(id+"F0.wireOp",EDGE,"E1.bottom");var subQ6=sQuery(id+"F0.wireOp",EDGE,"E21.filletArc");var subQ7=sQuery(id+"F0.wireOp",EDGE,"E1.top");var subQ8=sQuery(id+"F0.wireOp",EDGE,"E1.left");var subQ9=sQuery(id+"F0.wireOp",EDGE,"E1.right");var subQ10=sQuery(id+"F0.wireOp",EDGE,"E23.filletArc");var subQ11=sQuery(id+"F0.wireOp",EDGE,"E24.filletArc");Q0=makeQuery(id+"F2.boolean.opBoolean","SPLIT",FACE,{"disambiguationData":[TD([makeQuery(id+"F1.opExtrude","SWEPT_FACE",FACE,{"disambiguationData":[OSD([subQ5])]})])],"derivedFrom":makeQuery(id+"F1.opExtrude","CAP_FACE",FACE,{"disambiguationData":[OSD([subQ5,subQ7,subQ8,subQ9,subQ4,subQ3,subQ2,subQ1,subQ6,subQ0,subQ10,subQ11])],"isStart":true})});}
            var sketch = newSketch(context, id + "F16", { "sketchPlane" : qUnion([Q0])});
            skLineSegment(sketch, "E79", {"start": v(0, 74.25) * mm, "end": v(0, 94.98) * mm, "construction": true});
            skPoint(sketch, "E79.endSnap0", {"position": v(0, 74.25) * mm});
            skCircle(sketch, "E80", {"center": v(0, 94.98) * mm, "radius": 5.55 * mm});
            skLineSegment(sketch, "E81", {"start": v(-28.32, 74.25) * mm, "end": v(-14.87, 87.7) * mm});
            skLineSegment(sketch, "E82", {"start": v(-14.87, 87.7) * mm, "end": v(-14.87, 99.41) * mm});
            skLineSegment(sketch, "E83", {"start": v(28.58, 74.25) * mm, "end": v(15.13, 87.7) * mm});
            skLineSegment(sketch, "E84", {"start": v(15.13, 87.7) * mm, "end": v(15.13, 99.41) * mm});
            skArc(sketch, "E85", {"start": v(15.13, 99.41) * mm, "mid": v(0.13, 114.41) * mm, "end": v(-14.87, 99.41) * mm});
            skLineSegment(sketch, "E86", {"start": v(-74.25, 0) * mm, "end": v(74.25, 0) * mm, "construction": true});
            skPoint(sketch, "E87", {"position": v(-60, 60) * mm});
            skPoint(sketch, "E88", {"position": v(60, 60) * mm});
            skPoint(sketch, "E89", {"position": v(64.25, 64.25) * mm});
            skPoint(sketch, "E90", {"position": v(-64.25, 64.25) * mm});
            skPoint(sketch, "E91", {"position": v(-74.25, 64.25) * mm});
            skPoint(sketch, "E92", {"position": v(-64.25, 74.25) * mm});
            skPoint(sketch, "E93", {"position": v(-60, -60) * mm});
            skPoint(sketch, "E94", {"position": v(60, -60) * mm});
            skPoint(sketch, "E95", {"position": v(64.25, -64.25) * mm});
            skPoint(sketch, "E96", {"position": v(-64.25, -64.25) * mm});
            skPoint(sketch, "E97", {"position": v(-74.25, -64.25) * mm});
            skPoint(sketch, "E98", {"position": v(-64.25, -74.25) * mm});
            skPoint(sketch, "E99", {"position": v(60, -38.83) * mm});
            skPoint(sketch, "E100", {"position": v(54.26, -47.88) * mm});
            skPoint(sketch, "E101", {"position": v(50, -38.83) * mm});
            skPoint(sketch, "E102", {"position": v(-50, -38.83) * mm});
            skPoint(sketch, "E103", {"position": v(-60, -38.83) * mm});
            skPoint(sketch, "E104", {"position": v(-54.26, -47.88) * mm});
            skPoint(sketch, "E105", {"position": v(-54.26, 47.88) * mm});
            skPoint(sketch, "E106", {"position": v(-60, 38.83) * mm});
            skPoint(sketch, "E107", {"position": v(-50, 38.83) * mm});
            skPoint(sketch, "E108", {"position": v(64.25, 74.25) * mm});
            skPoint(sketch, "E109", {"position": v(74.25, 64.25) * mm});
            skPoint(sketch, "E110", {"position": v(54.26, 47.88) * mm});
            skPoint(sketch, "E111", {"position": v(60, 38.83) * mm});
            skPoint(sketch, "E112", {"position": v(50, 38.83) * mm});
            skPoint(sketch, "E113", {"position": v(74.25, 5.2) * mm});
            skPoint(sketch, "E114", {"position": v(0, -67.5) * mm});
            skLineSegment(sketch, "E115.MirrorCS", {"start": v(15.13, -87.7) * mm, "end": v(15.13, -99.41) * mm});
            skArc(sketch, "E116.MirrorCS", {"start": v(15.13, -99.41) * mm, "mid": v(0.13, -114.41) * mm, "end": v(-14.87, -99.41) * mm});
            skLineSegment(sketch, "E117.MirrorCS", {"start": v(-14.87, -87.7) * mm, "end": v(-14.87, -99.41) * mm});
            skLineSegment(sketch, "E118.MirrorCS", {"start": v(-28.32, -74.25) * mm, "end": v(-14.87, -87.7) * mm});
            skLineSegment(sketch, "E119.MirrorCS", {"start": v(28.58, -74.25) * mm, "end": v(15.13, -87.7) * mm});
            skLineSegment(sketch, "E120.MirrorCS", {"start": v(0, -74.25) * mm, "end": v(0, -94.98) * mm, "construction": true});
            skCircle(sketch, "E121.MirrorC", {"center": v(0, -94.98) * mm, "radius": 5.55 * mm});
            skSolve(sketch);
        }
        {
            var Q0;
            Q0=makeQuery(id+"F16.imprint","IMPRINT",FACE,{"disambiguationData":[TD([[makeQuery(id+"F16.imprint","IMPRINT",EDGE,{"derivedFrom":sQuery(id+"F16.wireOp",EDGE,"E80")}),-1.0]])]});
            var Q1;
            Q1=makeQuery(id+"F16.imprint","IMPRINT",FACE,{"disambiguationData":[TD([[makeQuery(id+"F16.imprint","IMPRINT",EDGE,{"derivedFrom":makeQuery(id+"F1.opExtrude","CAP_EDGE",EDGE,{"disambiguationData":[OSD([sQuery(id+"F0.wireOp",EDGE,"E1.left")])],"isStart":true})}),-1.0]])]});
            var Q2;
            Q2=makeQuery(id+"F16.imprint","IMPRINT",FACE,{"disambiguationData":[TD([[makeQuery(id+"F16.imprint","IMPRINT",EDGE,{"derivedFrom":sQuery(id+"F16.wireOp",EDGE,"E115.MirrorCS")}),-1.0]])]});
            var Q3;
            Q3=makeQuery(id+"F2.opExtrude","CAP_FACE",FACE,{"disambiguationData":[OSD([sQuery(id+"F0.wireOp",EDGE,"E12"),sQuery(id+"F0.wireOp",EDGE,"E13"),sQuery(id+"F0.wireOp",EDGE,"E14"),sQuery(id+"F0.wireOp",EDGE,"E15"),sQuery(id+"F0.wireOp",EDGE,"E17.filletArc"),sQuery(id+"F0.wireOp",EDGE,"E18.filletArc"),sQuery(id+"F0.wireOp",EDGE,"E19.filletArc"),sQuery(id+"F0.wireOp",EDGE,"E20.filletArc"),sQuery(id+"F0.wireOp",EDGE,"E25.0"),sQuery(id+"F0.wireOp",EDGE,"E25.1"),sQuery(id+"F0.wireOp",EDGE,"E25.2"),sQuery(id+"F0.wireOp",EDGE,"E25.3"),sQuery(id+"F0.wireOp",EDGE,"E25.4"),sQuery(id+"F0.wireOp",EDGE,"E25.5"),sQuery(id+"F0.wireOp",EDGE,"E25.6"),sQuery(id+"F0.wireOp",EDGE,"E25.7")])],"isStart":false});
            extrude(context, id + "F17", {"entities" : qUnion([Q0, Q1, Q2]), "endBound" : BoundingType.UP_TO_SURFACE, "endBoundEntityFace" : qUnion([Q3]), "depth" : 25 * mm});
        }
    });
